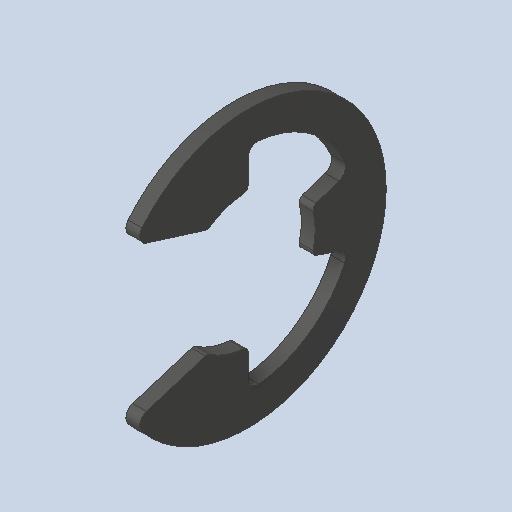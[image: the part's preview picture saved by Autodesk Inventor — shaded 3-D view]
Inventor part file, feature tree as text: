
AUTODESK INVENTOR PART (.ipt)
format: ipt  version: 2023 (Build 270158000, 158)  size: 113,152 bytes
history: native  units: in
note: dims shown in document units (in); Inventor stores cm internally (conversion verified against a paired STEP export)
features: fillet x1
ambient origin geometry x8: Origin, YZ Plane, XZ Plane, XY Plane, X Axis, Y Axis, Z Axis, Center Point
bodies: Solid1 (feature_tree)
feature tree (1):
  fillet  "Fillet2"  [1 undecoded]
note: 1 required parameter value undecoded (feature->parameter linkage not recoverable at this tier; creation-order binding heuristic only, values carry confidence <= 0.55)
